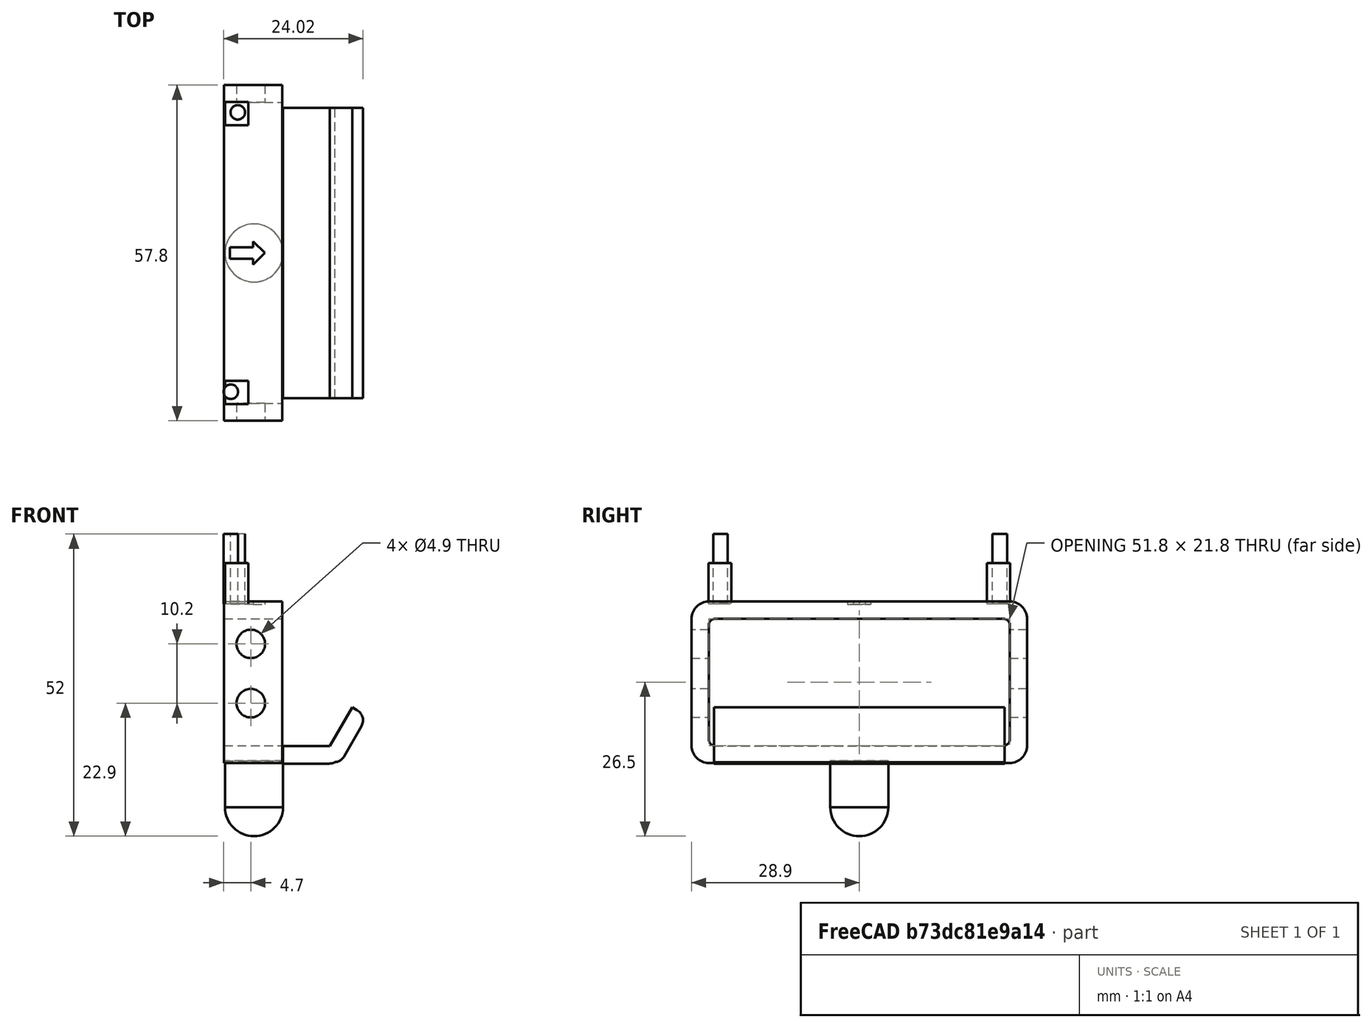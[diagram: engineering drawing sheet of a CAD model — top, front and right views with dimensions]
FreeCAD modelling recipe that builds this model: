
FCSTD DOCUMENT  (FreeCAD 0.17R13541 (Git))
Label: icelobot_b_v2
License: All rights reserved
LicenseURL: http://en.wikipedia.org/wiki/All_rights_reserved
objects: Part::Box×5, Part::Cylinder×3, Part::Fillet×2, Part::Feature×1, Part::MultiFuse×1, Part::Sphere×1, Part::Cut×1
note: 14 computed .brp shape members not serialized (recipe doc carries the construction recipe); baked Part::Feature solids carry a one-line shape summary decoded from their .brp

FEATURE [Part::Feature] Part__Feature  label="back"
  Placement = pos=(10.3,-35,-45) rot=(0,1,0;1.5708rad)
  shape: bbox 10 x 57.8 x 27.8 mm, 30 faces (baked)
FEATURE [Part::Cylinder] Cylinder  label="Cilindrob1"
  Angle = 360
  AttacherType = Attacher::AttachEngine3D
  Height = 12
  Placement = pos=(12.2,-10.8,-33) rot=(0,0,1;0rad)
  Radius = 1.25
FEATURE [Part::Cylinder] Cylinder001  label="Cilindrob2"
  Angle = 360
  AttacherType = Attacher::AttachEngine3D
  Height = 12
  Placement = pos=(11,-58.9,-33) rot=(0,0,1;0rad)
  Radius = 1.25
FEATURE [Part::Box] Box  label="Cubo"
  AttacherType = Attacher::AttachEngine3D
  Height = 3
  Length = 10
  Placement = pos=(30,-60,-60.5) rot=(0,-1,0;1.0472rad)
  Width = 50
FEATURE [Part::Box] Box001  label="Cubo001"
  AttacherType = Attacher::AttachEngine3D
  Height = 3
  Length = 10
  Placement = pos=(20,-60,-60.5) rot=(0,0,1;0rad)
  Width = 50
FEATURE [Part::Fillet] Fillet
  Base = -> Box
  Edges = 2 edges r=2: [Edge4,Edge8]
  Placement = pos=(-0.5,0,-0.5) rot=(0,0,1;0rad)
FEATURE [Part::Fillet] Fillet001
  Base = -> Box001
  Edges = 1 edges r=2: [Edge8]
FEATURE [Part::MultiFuse] Fusion  label="SoportePila"
  Shapes = -> [Fillet,Fillet001]
FEATURE [Part::Sphere] Sphere  label="Esfera"
  Angle1 = -90
  Angle2 = 90
  Angle3 = 360
  AttacherType = Attacher::AttachEngine3D
  Radius = 5
FEATURE [Part::Box] Box002  label="Cubo002"
  AttacherType = Attacher::AttachEngine3D
  Height = 10
  Length = 10
  Placement = pos=(-5,-5,0) rot=(0,0,1;0rad)
  Width = 10
FEATURE [Part::Cut] Cut
  Base = -> Sphere
  Placement = pos=(15,-35,-68) rot=(0,0,1;0rad)
  Tool = -> Box002
FEATURE [Part::Cylinder] Cylinder002  label="Cilindro"
  Angle = 360
  AttacherType = Attacher::AttachEngine3D
  Height = 8
  Placement = pos=(15,-35,-68) rot=(0,0,1;0rad)
  Radius = 5
FEATURE [Part::Box] Box003  label="Soprte Placa"
  AttacherType = Attacher::AttachEngine3D
  Height = 7
  Length = 4
  Placement = pos=(10,-13,-33) rot=(0,0,1;0rad)
  Width = 4
FEATURE [Part::Box] Box004  label="Soporte Placa2"
  AttacherType = Attacher::AttachEngine3D
  Height = 7
  Length = 4
  Placement = pos=(10,-61,-33) rot=(0,0,1;0rad)
  Width = 4
